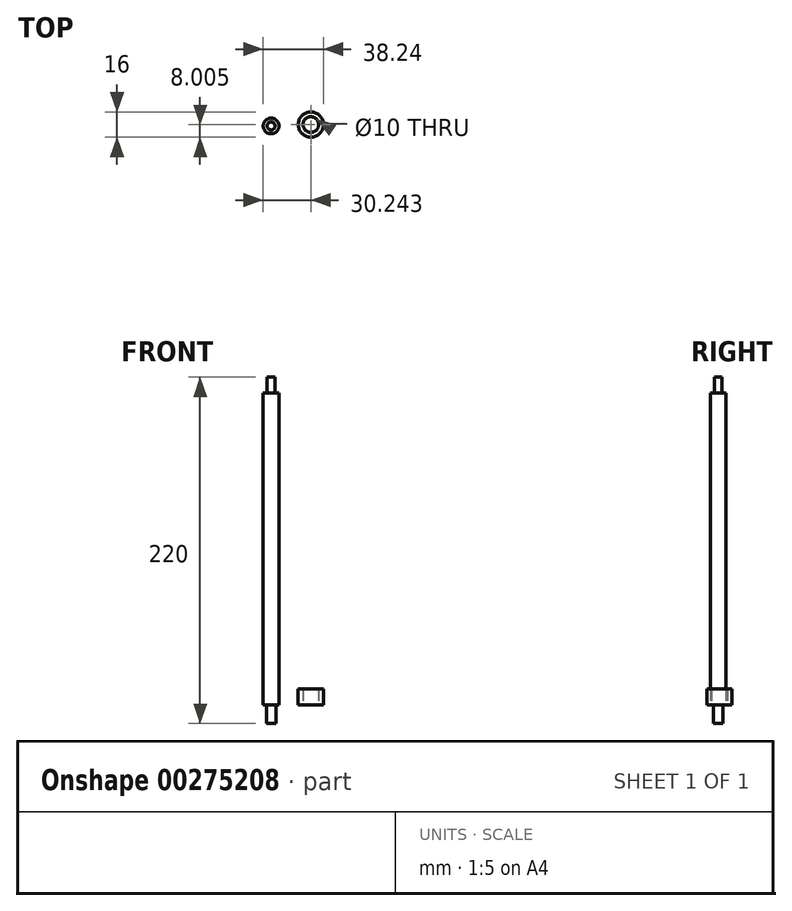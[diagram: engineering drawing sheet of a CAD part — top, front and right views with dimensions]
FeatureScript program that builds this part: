
annotation { "Feature Type Name" : "Feature", "Feature Type Description" : "" }
export const myFeature = defineFeature(function(context is Context, id is Id, definition is map)
    precondition{}
    {
        {
            var Q0;
            Q0=qCreatedBy(makeId("Top.planeOp"),FACE);
            var sketch = newSketch(context, id + "F0", { "sketchPlane" : qUnion([Q0])});
            skCircle(sketch, "E0", {"center": v(-24.98, 28.4) * mm, "radius": 5 * mm});
            skCircle(sketch, "E1", {"center": v(0.26, 29.27) * mm, "radius": 5 * mm});
            skCircle(sketch, "E2", {"center": v(0.26, 29.27) * mm, "radius": 8 * mm});
            skCircle(sketch, "E3", {"center": v(-24.98, 28.4) * mm, "radius": 3 * mm});
            skSolve(sketch);
        }
        {
            var Q0;
            Q0=makeQuery(id+"F0.imprint","IMPRINT",FACE,{"disambiguationData":[TD([[makeQuery(id+"F0.imprint","IMPRINT",EDGE,{"derivedFrom":sQuery(id+"F0.wireOp",EDGE,"E1")}),-1.0]])]});
            extrude(context, id + "F1", {"entities" : qUnion([Q0]), "depth" : 10 * mm});
        }
        {
            var Q0;
            Q0=makeQuery(id+"F0.imprint","IMPRINT",FACE,{"disambiguationData":[TD([[makeQuery(id+"F0.imprint","IMPRINT",EDGE,{"derivedFrom":sQuery(id+"F0.wireOp",EDGE,"E0")}),1.0]])]});
            var Q1;
            Q1=makeQuery(id+"F0.imprint","IMPRINT",FACE,{"disambiguationData":[TD([[makeQuery(id+"F0.imprint","IMPRINT",EDGE,{"derivedFrom":sQuery(id+"F0.wireOp",EDGE,"E3")}),1.0]])]});
            extrude(context, id + "F2", {"entities" : qUnion([Q0, Q1]), "flatOperationType" : FlatOperationType.REMOVE, "offsetDistance" : 25 * mm, "depth" : 208 * mm, "domain" : OperationDomain.MODEL});
        }
        {
            var Q0;
            Q0=makeQuery(id+"F0.imprint","IMPRINT",FACE,{"disambiguationData":[TD([[makeQuery(id+"F0.imprint","IMPRINT",EDGE,{"derivedFrom":sQuery(id+"F0.wireOp",EDGE,"E3")}),1.0]])]});
            extrude(context, id + "F3", {"entities" : qUnion([Q0]), "operationType" : NewBodyOperationType.ADD, "oppositeDirection" : true, "depth" : 12 * mm});
        }
        {
            var Q0;
            Q0=makeQuery(id+"F2.opExtrude","CAP_FACE",FACE,{"disambiguationData":[OSD([sQuery(id+"F0.wireOp",EDGE,"E0")])],"isStart":false});
            var sketch = newSketch(context, id + "F4", { "sketchPlane" : qUnion([Q0])});
            skPoint(sketch, "E4.0", {"position": v(-24.98, 28.4) * mm});
            skCircle(sketch, "E5", {"center": v(-24.98, 28.4) * mm, "radius": 2.5 * mm});
            skSolve(sketch);
        }
        {
            var Q0;
            Q0=makeQuery(id+"F4.imprint","IMPRINT",FACE,{"disambiguationData":[TD([[makeQuery(id+"F4.imprint","IMPRINT",EDGE,{"derivedFrom":sQuery(id+"F4.wireOp",EDGE,"E5")}),-1.0]])]});
            extrude(context, id + "F5", {"entities" : qUnion([Q0]), "operationType" : NewBodyOperationType.REMOVE, "oppositeDirection" : true, "depth" : 10 * mm});
        }
    });
